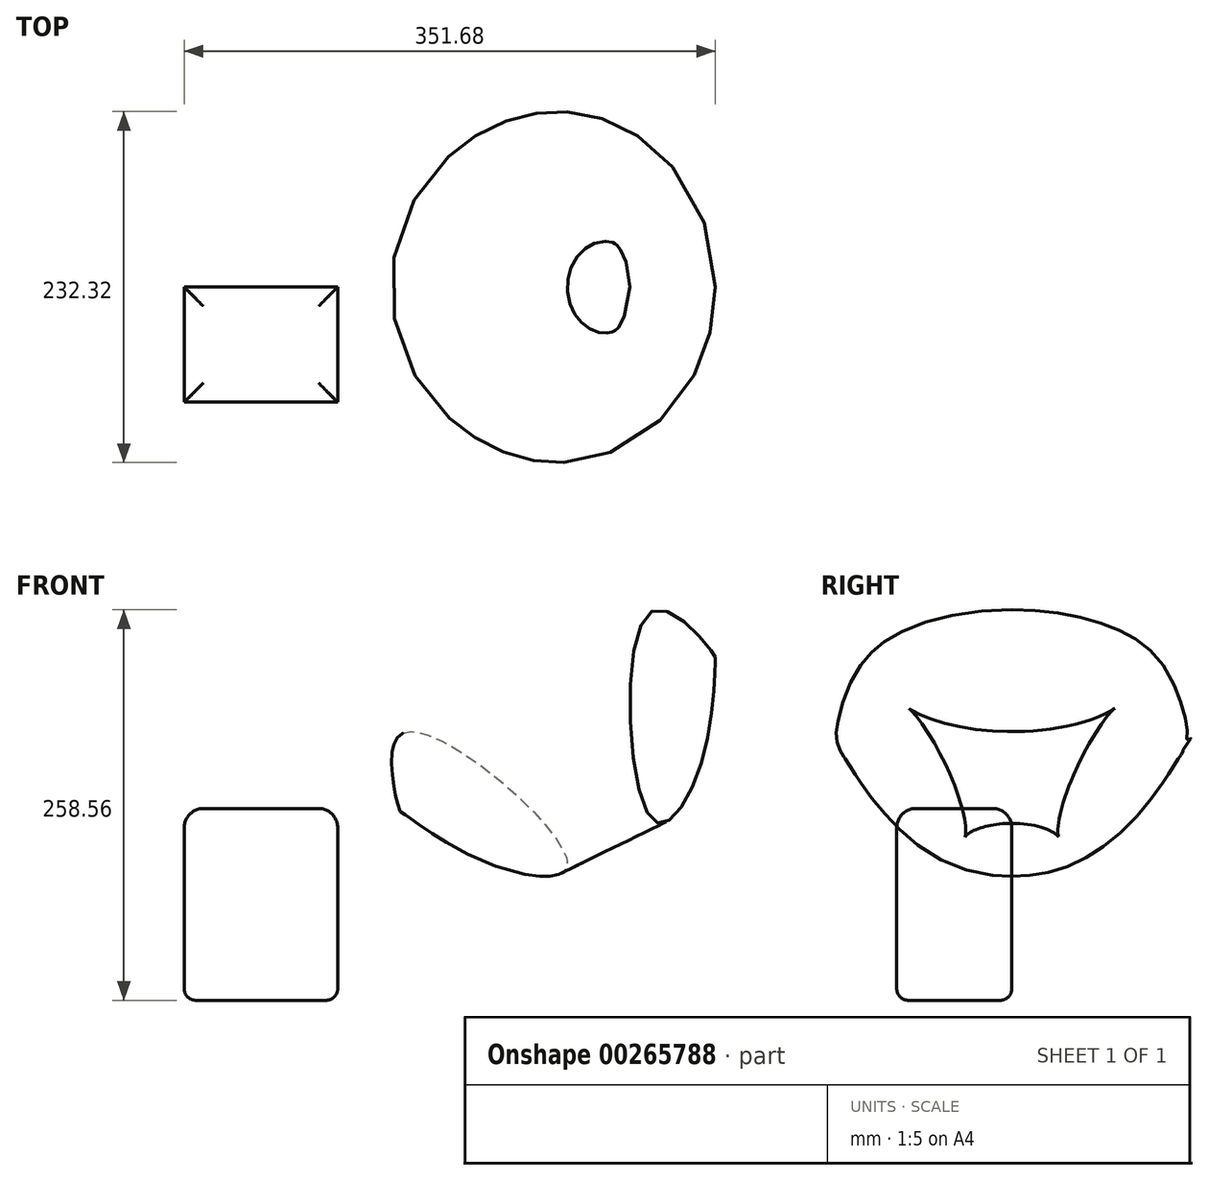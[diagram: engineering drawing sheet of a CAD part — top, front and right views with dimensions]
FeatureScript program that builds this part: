
annotation { "Feature Type Name" : "Feature", "Feature Type Description" : "" }
export const myFeature = defineFeature(function(context is Context, id is Id, definition is map)
    precondition{}
    {
        {
            var Q0;
            Q0=qCreatedBy(makeId("Front.planeOp"),FACE);
            var sketch = newSketch(context, id + "F0", { "sketchPlane" : qUnion([Q0])});
            skLineSegment(sketch, "E0.bottom", {"start": v(-309.73, -62.9) * mm, "end": v(-208.13, -62.9) * mm});
            skLineSegment(sketch, "E0.top", {"start": v(-309.73, -189.9) * mm, "end": v(-208.13, -189.9) * mm});
            skLineSegment(sketch, "E0.left", {"start": v(-309.73, -62.9) * mm, "end": v(-309.73, -189.9) * mm});
            skLineSegment(sketch, "E0.right", {"start": v(-208.13, -62.9) * mm, "end": v(-208.13, -189.9) * mm});
            skLineSegment(sketch, "E1", {"start": v(-118.1, 100) * mm, "end": v(-65.26, -8.03) * mm});
            skFitSpline(sketch, "E2", {"points": [v(0, 67.64) * mm, v(41.04, 38.8) * mm, v(41.84, 35.4) * mm, v(32.29, -33.46) * mm, v(0, -70.17) * mm, v(0, 67.64) * mm]});
            skSolve(sketch);
        }
        {
            var Q0;
            Q0=makeQuery(id+"F0.imprint","IMPRINT",FACE,{"disambiguationData":[TD([[makeQuery(id+"F0.imprint","IMPRINT",EDGE,{"derivedFrom":sQuery(id+"F0.wireOp",EDGE,"7b8582f3-9799-40ea-b846-d7638e694a5a")}),1.0]])]});
            var Q1;
            Q1=makeQuery(id+"F0.imprint","IMPRINT",FACE,{"disambiguationData":[TD([[makeQuery(id+"F0.imprint","IMPRINT",EDGE,{"derivedFrom":sQuery(id+"F0.wireOp",EDGE,"E2")}),-1.0]])]});
            var Q2;
            Q2=sQuery(id+"F0.wireOp",EDGE,"E1");
            revolve(context, id + "F1", {"entities" : qUnion([Q0, Q1]), "axis" : qUnion([Q2]), "revolveType" : RevolveType.FULL});
        }
        {
            var Q0;
            Q0=makeQuery(id+"F0.imprint","IMPRINT",FACE,{"disambiguationData":[TD([[makeQuery(id+"F0.imprint","IMPRINT",EDGE,{"derivedFrom":sQuery(id+"F0.wireOp",EDGE,"E0.bottom")}),-1.0]])]});
            extrude(context, id + "F2", {"entities" : qUnion([Q0]), "depth" : 76.2 * mm});
        }
        {
            var Q0;
            Q0=makeQuery(id+"F2.opExtrude","CAP_EDGE",EDGE,{"disambiguationData":[OSD([sQuery(id+"F0.wireOp",EDGE,"E0.bottom")])],"isStart":true});
            var Q1;
            Q1=makeQuery(id+"F2.opExtrude","SWEPT_EDGE",EDGE,{"disambiguationData":[OSD([sQuery(id+"F0.wireOp",EDGE,"E0.bottom"),sQuery(id+"F0.wireOp",EDGE,"E0.left")])]});
            var Q2;
            Q2=makeQuery(id+"F2.opExtrude","CAP_EDGE",EDGE,{"disambiguationData":[OSD([sQuery(id+"F0.wireOp",EDGE,"E0.bottom")])],"isStart":false});
            var Q3;
            Q3=makeQuery(id+"F2.opExtrude","SWEPT_EDGE",EDGE,{"disambiguationData":[OSD([sQuery(id+"F0.wireOp",EDGE,"E0.bottom"),sQuery(id+"F0.wireOp",EDGE,"E0.right")])]});
            fillet(context, id + "F3", {"entities" : qUnion([Q0, Q1, Q2, Q3]), "radius" : 12.7 * mm, "tangentPropagation" : true, "allowEdgeOverflow" : false});
        }
        {
            var Q0;
            Q0=makeQuery(id+"F2.opExtrude","CAP_EDGE",EDGE,{"disambiguationData":[OSD([sQuery(id+"F0.wireOp",EDGE,"E0.top")])],"isStart":false});
            var Q1;
            Q1=makeQuery(id+"F2.opExtrude","SWEPT_EDGE",EDGE,{"disambiguationData":[OSD([sQuery(id+"F0.wireOp",EDGE,"E0.top"),sQuery(id+"F0.wireOp",EDGE,"E0.left")])]});
            var Q2;
            Q2=makeQuery(id+"F2.opExtrude","CAP_EDGE",EDGE,{"disambiguationData":[OSD([sQuery(id+"F0.wireOp",EDGE,"E0.top")])],"isStart":true});
            var Q3;
            Q3=makeQuery(id+"F2.opExtrude","SWEPT_EDGE",EDGE,{"disambiguationData":[OSD([sQuery(id+"F0.wireOp",EDGE,"E0.top"),sQuery(id+"F0.wireOp",EDGE,"E0.right")])]});
            fillet(context, id + "F4", {"entities" : qUnion([Q0, Q1, Q2, Q3]), "radius" : 7.62 * mm, "tangentPropagation" : true, "allowEdgeOverflow" : false});
        }
    });
